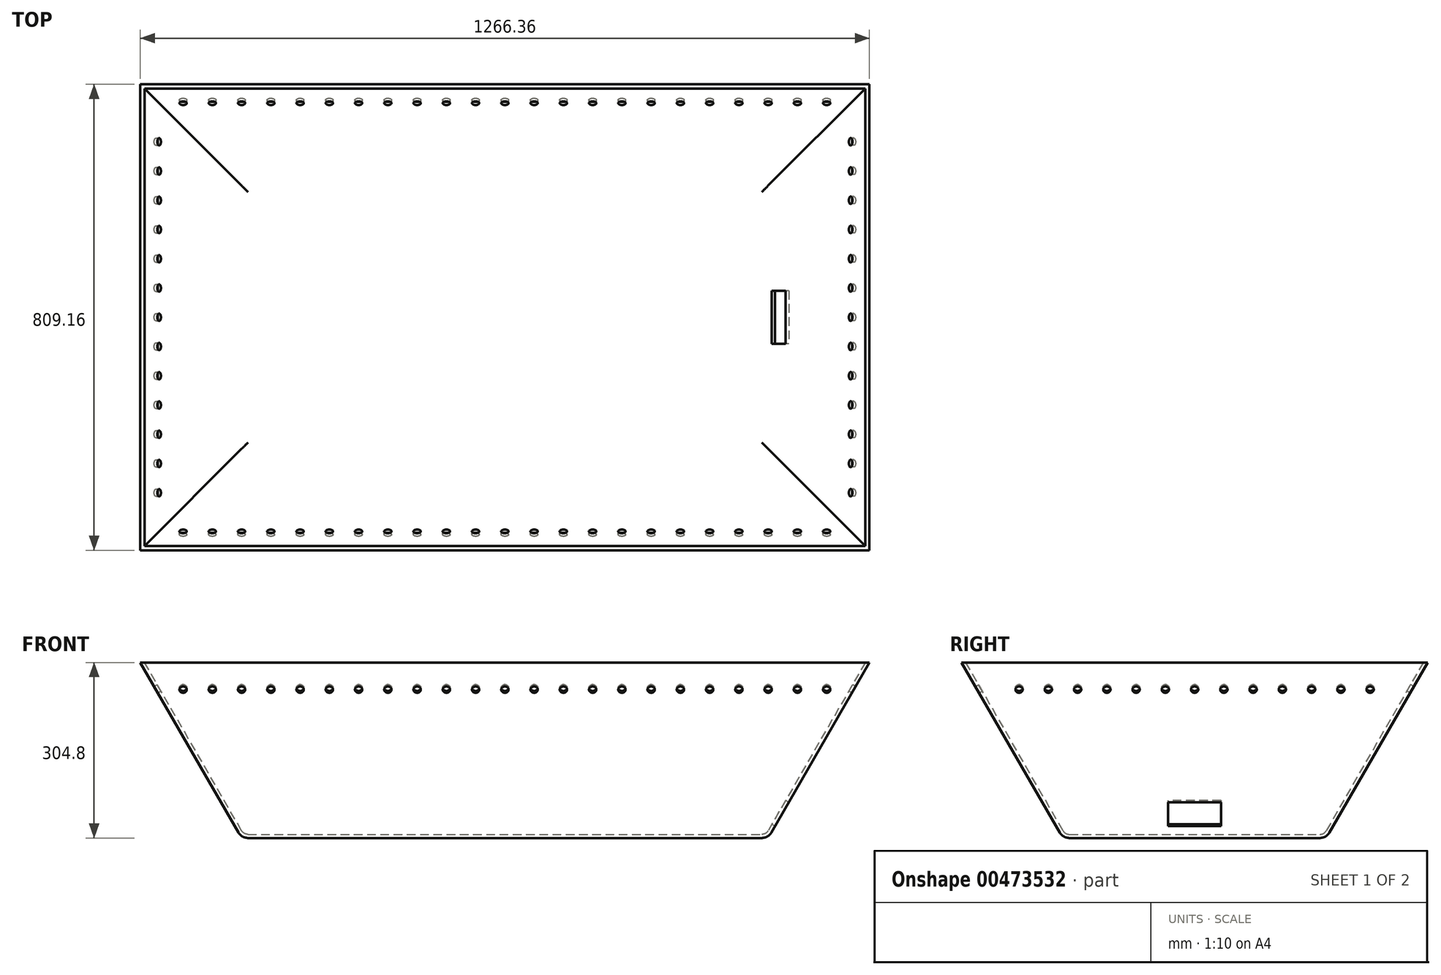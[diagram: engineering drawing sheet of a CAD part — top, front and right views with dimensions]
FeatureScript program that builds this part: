
annotation { "Feature Type Name" : "Feature", "Feature Type Description" : "" }
export const myFeature = defineFeature(function(context is Context, id is Id, definition is map)
    precondition{}
    {
        {
            var Q0;
            Q0=qCreatedBy(makeId("Top.planeOp"),FACE);
            var sketch = newSketch(context, id + "F0", { "sketchPlane" : qUnion([Q0])});
            skLineSegment(sketch, "E0.bottom", {"start": v(-457.2, -457.2) * mm, "end": v(457.2, -457.2) * mm});
            skLineSegment(sketch, "E0.top", {"start": v(-457.2, 0) * mm, "end": v(457.2, 0) * mm});
            skLineSegment(sketch, "E0.left", {"start": v(-457.2, -457.2) * mm, "end": v(-457.2, 0) * mm});
            skLineSegment(sketch, "E0.right", {"start": v(457.2, -457.2) * mm, "end": v(457.2, 0) * mm});
            skSolve(sketch);
        }
        {
            var Q0;
            Q0=makeQuery(id+"F0.imprint","IMPRINT",FACE,{"disambiguationData":[TD([[makeQuery(id+"F0.imprint","IMPRINT",EDGE,{"derivedFrom":sQuery(id+"F0.wireOp",EDGE,"E0.bottom")}),1.0]])]});
            extrude(context, id + "F1", {"entities" : qUnion([Q0]), "depth" : 304.8 * mm, "hasDraft" : true, "draftAngle" : 30 * degree});
        }
        {
            var Q0;
            Q0=makeQuery(id+"F1.opExtrude","CAP_FACE",FACE,{"disambiguationData":[OSD([sQuery(id+"F0.wireOp",EDGE,"E0.bottom"),sQuery(id+"F0.wireOp",EDGE,"E0.top"),sQuery(id+"F0.wireOp",EDGE,"E0.left"),sQuery(id+"F0.wireOp",EDGE,"E0.right")])],"isStart":false});
            shell(context, id + "F2", {"entities" : qUnion([Q0]), "thickness" : 6.35 * mm});
        }
        {
            var Q0;
            Q0=makeQuery(id+"F2.opShell","OFFSET_FACE",FACE,{"disambiguationData":[OSD([sQuery(id+"F0.wireOp",EDGE,"E0.top")])]});
            var sketch = newSketch(context, id + "F3", { "sketchPlane" : qUnion([Q0])});
            skLineSegment(sketch, "E1", {"start": v(-600.44, 297.49) * mm, "end": v(600.44, 297.49) * mm});
            skPoint(sketch, "E2", {"position": v(0, 297.49) * mm});
            skPoint(sketch, "E3.1.0.0", {"position": v(50.8, 297.49) * mm});
            skPoint(sketch, "E3.2.0.0", {"position": v(101.6, 297.49) * mm});
            skPoint(sketch, "E3.3.0.0", {"position": v(152.4, 297.49) * mm});
            skPoint(sketch, "E3.4.0.0", {"position": v(203.2, 297.49) * mm});
            skPoint(sketch, "E3.5.0.0", {"position": v(254, 297.49) * mm});
            skLineSegment(sketch, "E3.direction1", {"start": v(0, 297.49) * mm, "end": v(50.8, 297.49) * mm, "construction": true});
            skPoint(sketch, "E4.1.0.0", {"position": v(-50.8, 297.49) * mm});
            skPoint(sketch, "E4.2.0.0", {"position": v(-101.6, 297.49) * mm});
            skPoint(sketch, "E4.3.0.0", {"position": v(-152.4, 297.49) * mm});
            skPoint(sketch, "E4.4.0.0", {"position": v(-203.2, 297.49) * mm});
            skPoint(sketch, "E4.5.0.0", {"position": v(-254, 297.49) * mm});
            skLineSegment(sketch, "E4.direction1", {"start": v(0, 297.49) * mm, "end": v(-50.8, 297.49) * mm, "construction": true});
            skPoint(sketch, "E5.0.6.0", {"position": v(-304.8, 297.49) * mm});
            skPoint(sketch, "E5.0.7.0", {"position": v(-355.6, 297.49) * mm});
            skPoint(sketch, "E5.0.8.0", {"position": v(-406.4, 297.49) * mm});
            skPoint(sketch, "E5.0.9.0", {"position": v(-457.2, 297.49) * mm});
            skPoint(sketch, "E6.0.10.0", {"position": v(-508, 297.49) * mm});
            skPoint(sketch, "E6.0.11.0", {"position": v(-558.8, 297.49) * mm});
            skPoint(sketch, "E7.0.6.0", {"position": v(304.8, 297.49) * mm});
            skPoint(sketch, "E7.0.7.0", {"position": v(355.6, 297.49) * mm});
            skPoint(sketch, "E7.0.8.0", {"position": v(406.4, 297.49) * mm});
            skPoint(sketch, "E7.0.9.0", {"position": v(457.2, 297.49) * mm});
            skPoint(sketch, "E7.0.10.0", {"position": v(508, 297.49) * mm});
            skPoint(sketch, "E7.0.11.0", {"position": v(558.8, 297.49) * mm});
            skSolve(sketch);
        }
        {
            var Q0;
            Q0=makeQuery(id+"F2.opShell","OFFSET_FACE",FACE,{"disambiguationData":[OSD([sQuery(id+"F0.wireOp",EDGE,"E0.bottom")])]});
            var sketch = newSketch(context, id + "F4", { "sketchPlane" : qUnion([Q0])});
            skLineSegment(sketch, "E8", {"start": v(-600.44, 526.09) * mm, "end": v(600.44, 526.09) * mm});
            skPoint(sketch, "E9", {"position": v(0, 526.09) * mm});
            skPoint(sketch, "E10.1.0.0", {"position": v(50.8, 526.09) * mm});
            skPoint(sketch, "E10.2.0.0", {"position": v(101.6, 526.09) * mm});
            skPoint(sketch, "E10.3.0.0", {"position": v(152.4, 526.09) * mm});
            skPoint(sketch, "E10.4.0.0", {"position": v(203.2, 526.09) * mm});
            skPoint(sketch, "E10.5.0.0", {"position": v(254, 526.09) * mm});
            skLineSegment(sketch, "E10.direction1", {"start": v(0, 526.09) * mm, "end": v(50.8, 526.09) * mm, "construction": true});
            skPoint(sketch, "E11.1.0.0", {"position": v(-50.8, 526.09) * mm});
            skPoint(sketch, "E11.2.0.0", {"position": v(-101.6, 526.09) * mm});
            skPoint(sketch, "E11.3.0.0", {"position": v(-152.4, 526.09) * mm});
            skPoint(sketch, "E11.4.0.0", {"position": v(-203.2, 526.09) * mm});
            skPoint(sketch, "E11.5.0.0", {"position": v(-254, 526.09) * mm});
            skLineSegment(sketch, "E11.direction1", {"start": v(0, 526.09) * mm, "end": v(-50.8, 526.09) * mm, "construction": true});
            skPoint(sketch, "E12.0.6.0", {"position": v(304.8, 526.09) * mm});
            skPoint(sketch, "E12.0.7.0", {"position": v(355.6, 526.09) * mm});
            skPoint(sketch, "E12.0.8.0", {"position": v(406.4, 526.09) * mm});
            skPoint(sketch, "E12.0.9.0", {"position": v(457.2, 526.09) * mm});
            skPoint(sketch, "E12.0.10.0", {"position": v(508, 526.09) * mm});
            skPoint(sketch, "E12.0.11.0", {"position": v(558.8, 526.09) * mm});
            skPoint(sketch, "E13.0.6.0", {"position": v(-304.8, 526.09) * mm});
            skPoint(sketch, "E13.0.7.0", {"position": v(-355.6, 526.09) * mm});
            skPoint(sketch, "E13.0.8.0", {"position": v(-406.4, 526.09) * mm});
            skPoint(sketch, "E13.0.9.0", {"position": v(-457.2, 526.09) * mm});
            skPoint(sketch, "E13.0.10.0", {"position": v(-508, 526.09) * mm});
            skPoint(sketch, "E13.0.11.0", {"position": v(-558.8, 526.09) * mm});
            skSolve(sketch);
        }
        {
            var Q0;
            Q0=makeQuery(id+"F2.opShell","OFFSET_FACE",FACE,{"disambiguationData":[OSD([sQuery(id+"F0.wireOp",EDGE,"E0.left")])]});
            var sketch = newSketch(context, id + "F5", { "sketchPlane" : qUnion([Q0])});
            skLineSegment(sketch, "E14", {"start": v(143.24, 526.09) * mm, "end": v(-600.44, 526.09) * mm});
            skPoint(sketch, "E15", {"position": v(-228.6, 526.09) * mm});
            skPoint(sketch, "E16.1.0.0", {"position": v(-177.8, 526.09) * mm});
            skPoint(sketch, "E16.2.0.0", {"position": v(-127, 526.09) * mm});
            skPoint(sketch, "E16.3.0.0", {"position": v(-76.2, 526.09) * mm});
            skPoint(sketch, "E16.4.0.0", {"position": v(-25.4, 526.09) * mm});
            skPoint(sketch, "E16.5.0.0", {"position": v(25.4, 526.09) * mm});
            skPoint(sketch, "E16.6.0.0", {"position": v(76.2, 526.09) * mm});
            skLineSegment(sketch, "E16.direction1", {"start": v(-228.6, 526.09) * mm, "end": v(-177.8, 526.09) * mm, "construction": true});
            skPoint(sketch, "E17.0.7.0", {"position": v(127, 526.09) * mm});
            skPoint(sketch, "E18.1.0.0", {"position": v(-279.4, 526.09) * mm});
            skPoint(sketch, "E18.2.0.0", {"position": v(-330.2, 526.09) * mm});
            skPoint(sketch, "E18.3.0.0", {"position": v(-381, 526.09) * mm});
            skPoint(sketch, "E18.4.0.0", {"position": v(-431.8, 526.09) * mm});
            skPoint(sketch, "E18.5.0.0", {"position": v(-482.6, 526.09) * mm});
            skPoint(sketch, "E18.6.0.0", {"position": v(-533.4, 526.09) * mm});
            skPoint(sketch, "E18.7.0.0", {"position": v(-584.2, 526.09) * mm});
            skLineSegment(sketch, "E18.direction1", {"start": v(-228.6, 526.09) * mm, "end": v(-279.4, 526.09) * mm, "construction": true});
            skSolve(sketch);
        }
        {
            var Q0;
            Q0=makeQuery(id+"F2.opShell","OFFSET_FACE",FACE,{"disambiguationData":[OSD([sQuery(id+"F0.wireOp",EDGE,"E0.right")])]});
            var sketch = newSketch(context, id + "F6", { "sketchPlane" : qUnion([Q0])});
            skLineSegment(sketch, "E19", {"start": v(-143.24, 526.09) * mm, "end": v(600.44, 526.09) * mm});
            skPoint(sketch, "E20", {"position": v(228.6, 526.09) * mm});
            skPoint(sketch, "E21.1.0.0", {"position": v(279.4, 526.09) * mm});
            skPoint(sketch, "E21.2.0.0", {"position": v(330.2, 526.09) * mm});
            skPoint(sketch, "E21.3.0.0", {"position": v(381, 526.09) * mm});
            skPoint(sketch, "E21.4.0.0", {"position": v(431.8, 526.09) * mm});
            skPoint(sketch, "E21.5.0.0", {"position": v(482.6, 526.09) * mm});
            skPoint(sketch, "E21.6.0.0", {"position": v(533.4, 526.09) * mm});
            skPoint(sketch, "E21.7.0.0", {"position": v(584.2, 526.09) * mm});
            skLineSegment(sketch, "E21.direction1", {"start": v(228.6, 526.09) * mm, "end": v(279.4, 526.09) * mm, "construction": true});
            skPoint(sketch, "E22.1.0.0", {"position": v(177.8, 526.09) * mm});
            skPoint(sketch, "E22.2.0.0", {"position": v(127, 526.09) * mm});
            skPoint(sketch, "E22.3.0.0", {"position": v(76.2, 526.09) * mm});
            skPoint(sketch, "E22.4.0.0", {"position": v(25.4, 526.09) * mm});
            skPoint(sketch, "E22.5.0.0", {"position": v(-25.4, 526.09) * mm});
            skPoint(sketch, "E22.6.0.0", {"position": v(-76.2, 526.09) * mm});
            skPoint(sketch, "E22.7.0.0", {"position": v(-127, 526.09) * mm});
            skLineSegment(sketch, "E22.direction1", {"start": v(228.6, 526.09) * mm, "end": v(177.8, 526.09) * mm, "construction": true});
            skSolve(sketch);
        }
        {
            var Q0;
            Q0=sQuery(id+"F3.wireOp",VERTEX,"E2");
            var Q1;
            Q1=sQuery(id+"F3.wireOp",VERTEX,"E3.1.0.0");
            var Q2;
            Q2=sQuery(id+"F3.wireOp",VERTEX,"E3.2.0.0");
            var Q3;
            Q3=sQuery(id+"F3.wireOp",VERTEX,"E3.3.0.0");
            var Q4;
            Q4=sQuery(id+"F3.wireOp",VERTEX,"E3.4.0.0");
            var Q5;
            Q5=sQuery(id+"F3.wireOp",VERTEX,"E3.5.0.0");
            var Q6;
            Q6=sQuery(id+"F3.wireOp",VERTEX,"E4.1.0.0");
            var Q7;
            Q7=sQuery(id+"F3.wireOp",VERTEX,"E4.2.0.0");
            var Q8;
            Q8=sQuery(id+"F3.wireOp",VERTEX,"E4.3.0.0");
            var Q9;
            Q9=sQuery(id+"F3.wireOp",VERTEX,"E4.4.0.0");
            var Q10;
            Q10=sQuery(id+"F3.wireOp",VERTEX,"E4.5.0.0");
            var Q11;
            Q11=sQuery(id+"F4.wireOp",VERTEX,"E11.5.0.0");
            var Q12;
            Q12=sQuery(id+"F4.wireOp",VERTEX,"E11.4.0.0");
            var Q13;
            Q13=sQuery(id+"F4.wireOp",VERTEX,"E11.3.0.0");
            var Q14;
            Q14=sQuery(id+"F4.wireOp",VERTEX,"E11.2.0.0");
            var Q15;
            Q15=sQuery(id+"F4.wireOp",VERTEX,"E11.1.0.0");
            var Q16;
            Q16=sQuery(id+"F4.wireOp",VERTEX,"E9");
            var Q17;
            Q17=sQuery(id+"F4.wireOp",VERTEX,"E10.1.0.0");
            var Q18;
            Q18=sQuery(id+"F4.wireOp",VERTEX,"E10.2.0.0");
            var Q19;
            Q19=sQuery(id+"F4.wireOp",VERTEX,"E10.3.0.0");
            var Q20;
            Q20=sQuery(id+"F4.wireOp",VERTEX,"E10.4.0.0");
            var Q21;
            Q21=sQuery(id+"F4.wireOp",VERTEX,"E10.5.0.0");
            var Q22;
            Q22=sQuery(id+"F3.wireOp",VERTEX,"E7.0.10.0");
            var Q23;
            Q23=sQuery(id+"F3.wireOp",VERTEX,"E7.0.6.0");
            var Q24;
            Q24=sQuery(id+"F3.wireOp",VERTEX,"E7.0.7.0");
            var Q25;
            Q25=sQuery(id+"F3.wireOp",VERTEX,"E7.0.9.0");
            var Q26;
            Q26=sQuery(id+"F3.wireOp",VERTEX,"E7.0.8.0");
            var Q27;
            Q27=sQuery(id+"F3.wireOp",VERTEX,"E7.0.11.0");
            var Q28;
            Q28=sQuery(id+"F3.wireOp",VERTEX,"E5.0.9.0");
            var Q29;
            Q29=sQuery(id+"F3.wireOp",VERTEX,"E6.0.11.0");
            var Q30;
            Q30=sQuery(id+"F3.wireOp",VERTEX,"E6.0.10.0");
            var Q31;
            Q31=sQuery(id+"F3.wireOp",VERTEX,"E5.0.8.0");
            var Q32;
            Q32=sQuery(id+"F3.wireOp",VERTEX,"E5.0.6.0");
            var Q33;
            Q33=sQuery(id+"F3.wireOp",VERTEX,"E5.0.7.0");
            var Q34;
            Q34=sQuery(id+"F4.wireOp",VERTEX,"E13.0.6.0");
            var Q35;
            Q35=sQuery(id+"F4.wireOp",VERTEX,"E13.0.7.0");
            var Q36;
            Q36=sQuery(id+"F4.wireOp",VERTEX,"E13.0.8.0");
            var Q37;
            Q37=sQuery(id+"F4.wireOp",VERTEX,"E13.0.9.0");
            var Q38;
            Q38=sQuery(id+"F4.wireOp",VERTEX,"E13.0.10.0");
            var Q39;
            Q39=sQuery(id+"F4.wireOp",VERTEX,"E13.0.11.0");
            var Q40;
            Q40=sQuery(id+"F4.wireOp",VERTEX,"E12.0.9.0");
            var Q41;
            Q41=sQuery(id+"F4.wireOp",VERTEX,"E12.0.11.0");
            var Q42;
            Q42=sQuery(id+"F4.wireOp",VERTEX,"E12.0.11.0");
            var Q43;
            Q43=sQuery(id+"F4.wireOp",VERTEX,"E12.0.10.0");
            var Q44;
            Q44=sQuery(id+"F4.wireOp",VERTEX,"E12.0.8.0");
            var Q45;
            Q45=sQuery(id+"F4.wireOp",VERTEX,"E12.0.7.0");
            var Q46;
            Q46=sQuery(id+"F4.wireOp",VERTEX,"E12.0.6.0");
            var Q47;
            Q47=sQuery(id+"F5.wireOp",VERTEX,"E18.6.0.0");
            var Q48;
            Q48=sQuery(id+"F5.wireOp",VERTEX,"E18.5.0.0");
            var Q49;
            Q49=sQuery(id+"F5.wireOp",VERTEX,"E18.4.0.0");
            var Q50;
            Q50=sQuery(id+"F5.wireOp",VERTEX,"E18.3.0.0");
            var Q51;
            Q51=sQuery(id+"F5.wireOp",VERTEX,"E18.2.0.0");
            var Q52;
            Q52=sQuery(id+"F5.wireOp",VERTEX,"E18.direction1.end");
            var Q53;
            Q53=sQuery(id+"F5.wireOp",VERTEX,"E15");
            var Q54;
            Q54=sQuery(id+"F5.wireOp",VERTEX,"E16.1.0.0");
            var Q55;
            Q55=sQuery(id+"F5.wireOp",VERTEX,"E16.2.0.0");
            var Q56;
            Q56=sQuery(id+"F5.wireOp",VERTEX,"E16.3.0.0");
            var Q57;
            Q57=sQuery(id+"F5.wireOp",VERTEX,"E16.4.0.0");
            var Q58;
            Q58=sQuery(id+"F5.wireOp",VERTEX,"E16.5.0.0");
            var Q59;
            Q59=sQuery(id+"F5.wireOp",VERTEX,"E16.6.0.0");
            var Q60;
            Q60=sQuery(id+"F6.wireOp",VERTEX,"E22.6.0.0");
            var Q61;
            Q61=sQuery(id+"F6.wireOp",VERTEX,"E22.5.0.0");
            var Q62;
            Q62=sQuery(id+"F6.wireOp",VERTEX,"E22.4.0.0");
            var Q63;
            Q63=sQuery(id+"F6.wireOp",VERTEX,"E22.3.0.0");
            var Q64;
            Q64=sQuery(id+"F6.wireOp",VERTEX,"E22.2.0.0");
            var Q65;
            Q65=sQuery(id+"F6.wireOp",VERTEX,"E22.1.0.0");
            var Q66;
            Q66=sQuery(id+"F6.wireOp",VERTEX,"E20");
            var Q67;
            Q67=sQuery(id+"F6.wireOp",VERTEX,"E21.1.0.0");
            var Q68;
            Q68=sQuery(id+"F6.wireOp",VERTEX,"E21.2.0.0");
            var Q69;
            Q69=sQuery(id+"F6.wireOp",VERTEX,"E21.3.0.0");
            var Q70;
            Q70=sQuery(id+"F6.wireOp",VERTEX,"E21.4.0.0");
            var Q71;
            Q71=sQuery(id+"F6.wireOp",VERTEX,"E21.5.0.0");
            var Q72;
            Q72=sQuery(id+"F6.wireOp",VERTEX,"E21.6.0.0");
            var Q73;
            Q73=makeQuery(id+"F1.opExtrude","SWEPT_BODY",BODY,{"disambiguationData":[OSD([sQuery(id+"F0.wireOp",EDGE,"E0.bottom"),sQuery(id+"F0.wireOp",EDGE,"E0.top"),sQuery(id+"F0.wireOp",EDGE,"E0.left"),sQuery(id+"F0.wireOp",EDGE,"E0.right")])]});
            hole(context, id + "F7", {"style" : HoleStyle.SIMPLE, "endStyle" : HoleEndStyle.THROUGH, "holeDiameter" : 12.7 * mm, "isTappedThrough" : true, "tappedDepth" : 12.7 * mm, "tapClearance" : 3, "locations" : qUnion([Q0, Q1, Q2, Q3, Q4, Q5, Q6, Q7, Q8, Q9, Q10, Q11, Q12, Q13, Q14, Q15, Q16, Q17, Q18, Q19, Q20, Q21, Q22, Q23, Q24, Q25, Q26, Q27, Q28, Q29, Q30, Q31, Q32, Q33, Q34, Q35, Q36, Q37, Q38, Q39, Q40, Q41, Q42, Q43, Q44, Q45, Q46, Q47, Q48, Q49, Q50, Q51, Q52, Q53, Q54, Q55, Q56, Q57, Q58, Q59, Q60, Q61, Q62, Q63, Q64, Q65, Q66, Q67, Q68, Q69, Q70, Q71, Q72]), "scope" : qUnion([Q73])});
        }
        {
            var Q0;
            {var subQ0=sQuery(id+"F0.wireOp",EDGE,"E0.right");Q0=makeQuery(id+"F2.opShell","OFFSET_EDGE",EDGE,{"disambiguationData":[OSD([subQ0]),TDD([makeQuery(id+"F1.opExtrude","CAP_EDGE",EDGE,{"disambiguationData":[OSD([subQ0])],"isStart":true})])]});}
            var Q1;
            {var subQ0=sQuery(id+"F0.wireOp",EDGE,"E0.top");Q1=makeQuery(id+"F2.opShell","OFFSET_EDGE",EDGE,{"disambiguationData":[OSD([subQ0]),TDD([makeQuery(id+"F1.opExtrude","CAP_EDGE",EDGE,{"disambiguationData":[OSD([subQ0])],"isStart":true})])]});}
            var Q2;
            {var subQ0=sQuery(id+"F0.wireOp",EDGE,"E0.bottom");Q2=makeQuery(id+"F2.opShell","OFFSET_EDGE",EDGE,{"disambiguationData":[OSD([subQ0]),TDD([makeQuery(id+"F1.opExtrude","CAP_EDGE",EDGE,{"disambiguationData":[OSD([subQ0])],"isStart":true})])]});}
            var Q3;
            {var subQ0=sQuery(id+"F0.wireOp",EDGE,"E0.left");Q3=makeQuery(id+"F2.opShell","OFFSET_EDGE",EDGE,{"disambiguationData":[OSD([subQ0]),TDD([makeQuery(id+"F1.opExtrude","CAP_EDGE",EDGE,{"disambiguationData":[OSD([subQ0])],"isStart":true})])]});}
            fillet(context, id + "F8", {"entities" : qUnion([Q0, Q1, Q2, Q3]), "radius" : 12.7 * mm, "tangentPropagation" : true, "allowEdgeOverflow" : false});
        }
        {
            var Q0;
            Q0=makeQuery(id+"F1.opExtrude","CAP_EDGE",EDGE,{"disambiguationData":[OSD([sQuery(id+"F0.wireOp",EDGE,"E0.left")])],"isStart":true});
            var Q1;
            Q1=makeQuery(id+"F1.opExtrude","CAP_EDGE",EDGE,{"disambiguationData":[OSD([sQuery(id+"F0.wireOp",EDGE,"E0.top")])],"isStart":true});
            var Q2;
            Q2=makeQuery(id+"F1.opExtrude","CAP_EDGE",EDGE,{"disambiguationData":[OSD([sQuery(id+"F0.wireOp",EDGE,"E0.bottom")])],"isStart":true});
            var Q3;
            Q3=makeQuery(id+"F1.opExtrude","CAP_EDGE",EDGE,{"disambiguationData":[OSD([sQuery(id+"F0.wireOp",EDGE,"E0.right")])],"isStart":true});
            fillet(context, id + "F9", {"entities" : qUnion([Q0, Q1, Q2, Q3]), "radius" : 19.05 * mm, "tangentPropagation" : true, "allowEdgeOverflow" : false});
        }
        {
            var Q0;
            Q0=makeQuery(id+"F2.opShell","OFFSET_FACE",FACE,{"disambiguationData":[OSD([sQuery(id+"F0.wireOp",EDGE,"E0.right")])]});
            var sketch = newSketch(context, id + "F10", { "sketchPlane" : qUnion([Q0])});
            skLineSegment(sketch, "E23.bottom", {"start": v(182.56, 300.09) * mm, "end": v(274.64, 300.09) * mm});
            skLineSegment(sketch, "E23.top", {"start": v(182.56, 252.43) * mm, "end": v(274.64, 252.43) * mm});
            skLineSegment(sketch, "E23.left", {"start": v(182.56, 300.09) * mm, "end": v(182.56, 252.43) * mm});
            skLineSegment(sketch, "E23.right", {"start": v(274.64, 300.09) * mm, "end": v(274.64, 252.43) * mm});
            skSolve(sketch);
        }
        {
            var Q0;
            Q0=makeQuery(id+"F10.imprint","IMPRINT",FACE,{"disambiguationData":[TD([[makeQuery(id+"F10.imprint","IMPRINT",EDGE,{"derivedFrom":sQuery(id+"F10.wireOp",EDGE,"E23.bottom")}),-1.0]])]});
            var Q1;
            Q1=makeQuery(id+"F1.opExtrude","SWEPT_FACE",FACE,{"disambiguationData":[OSD([sQuery(id+"F0.wireOp",EDGE,"E0.right")])]});
            extrude(context, id + "F11", {"entities" : qUnion([Q0]), "operationType" : NewBodyOperationType.REMOVE, "endBound" : BoundingType.UP_TO_SURFACE, "oppositeDirection" : true, "endBoundEntityFace" : qUnion([Q1]), "depth" : 25.4 * mm});
        }
    });
